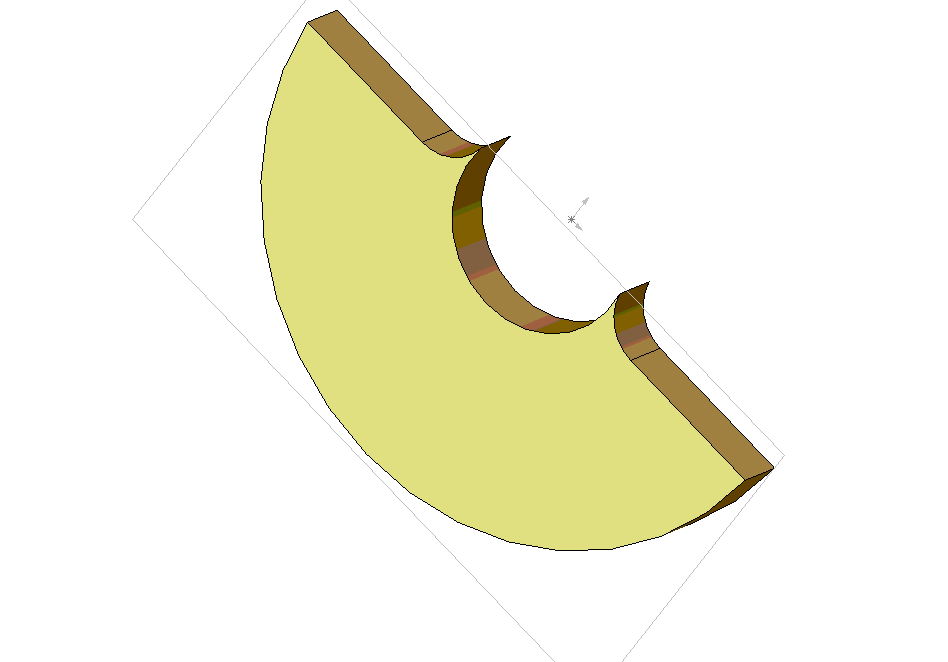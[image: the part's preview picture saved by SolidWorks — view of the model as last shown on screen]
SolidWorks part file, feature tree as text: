
SOLIDWORKS PART (.sldprt)
format: sldprt  version: not decoded by parser v0  size: 122,880 bytes
history: native  units: mm
features: sketch x3, extrude x2, plane x2, material x1, cut_extrude x1 (+12 scaffold rows collapsed)
feature tree (21):
  scaffold x12  (default folders/planes/origin — collapsed)
  material  "Material <not specified>"
  sketch  "Sketch1"  dims[D1=50.0mm D2=16.0mm]
  extrude  "Base-Extrude"  Depth=4.4mm
  plane  "Plane1"  Offset=0mm
  sketch  "Sketch2"  dims[D1=2.2mm]
  cut_extrude  "Cut-Extrude1"  [1 undecoded]
  plane  "Plane2"  Offset=0mm
  sketch  "Sketch3"  dims[D1=16.0mm D3=8.0mm D4=8.0mm D2=2.2mm]
  extrude  "Boss-Extrude1"  Depth=4.4mm
decode coverage: 5 of 6 modeling features carry decoded parameters
note: 1 parameter value undecoded
note: suppression state not decoded; provenance and decode notes live in map.json
